# Revit family: PRD_AR_HndSntzrDspnsrs_MEDCAREDispenser_MEDC10S_MEDC10L 2
name_source: partatom
category: Specialty Equipment
units: mm (PartAtom-declared; Revit-internal decimal feet)

## family parameters
Cut with Voids When Loaded = No
Enable Cutting in Views = No
Host = Face
Maintain Annotation Orientation = No
OmniClass Number = 23.40.20.21.34
OmniClass Title = Soap Holders, Dispensers
Part Type = Normal
Room Calculation Point = No
Round Connector Dimension = Use Diameter
Shared = No

## types (2) — shared parameters
AccentColour = grey
AssetType = Fixed
BasicColour = stainless steel-look
BodyMaterial = PRD_AR_Plastic_Grey
Category = Pr_40_70_22_35, Hand sanitizer dispensers
Color = grey
Colour = grey
ContainerMaterial = PRD_AR_Plastic_White
Default Elevation = 1050 mm
Export Type to IFC As = IfcSanitaryTerminalType
FillingQuantity = 1000
FillingQuantityUOM = ml
Finish = satin finished
HousingMaterial = PRD_AR_StainlessSteel_SatinFinished
IfcExportAs = IfcSanitaryTerminalType
IfcExportType = USERDEFINED
LeverMaterial = PRD_AR_StainlessSteel_HighPolished
Manufacturer = KWC Group Management AG
ManufacturerName = KWC Group Management AG
ManufacturerURL = www.kwc-professional.com
Material = stainless steel
MaterialCode = 1.4301 Chrome Nickel steel V2A
MaterialThickness = 1.25 mm
NBSDescription = Hand sanitizer dispensers
NBSReference = 45-35-72/333
NominalWidth = 94 mm  [stored 0.308399 ft]
OverallWidth = 94 mm
ProductInformation = http://pim.kwc.com
Status = New
SurfaceFinish = satin finished
Type IFC Predefined Type = USERDEFINED
TypeOfConsumable = disinfectant and liquid soap
TypeOfFixing = screw
TypeOfMounting = wall mounting
TypeOfOperation = manual operation
URL = www.kwc-professional.com
Uniclass2015Code = Pr_40_70_22_35
Uniclass2015Title = Hand sanitizer dispensers
Uniclass2015Version = Products v1.38
Version = 1

## per-type parameters (varying)
| type | BIMObjectName | Description | Features | MEDC10L | MEDC10S | ModelNumber | Name | NominalDepth | NominalHeight | NominalLength | OverallDepth | OverallHeight | Size |
| MEDC10L | PRD_AR_HandSanitizerDispensers_MEDCAREDispenser_MEDC10L | MEDCARE dispenser for liquid soaps and disinfectants, for wall mounting, stainless steel housing (dishwasher safe up to 60 °C), satin finished surface, material thickness 1.25 mm, grey plastic outlet cover, for 1000 ml standard Euro-bottles to be provided by the client, with stainless steel operating lever 230 mm, including wall bracket and mounting material. | For liquid soaps and disinfectants for wall mounting, stainless steel housing. With stainless steel operating lever 230 mm. Disposable pump must be ordered separately. | Yes | No | 3600003341 | MEDCARE Dispenser for liquid soaps and disinfectants MEDC10L | 230 mm  [stored 0.754593 ft] | 321 mm  [stored 1.05315 ft] | 321 mm  [stored 1.05315 ft] | 230 mm | 321 mm | 94 x 321 x 230 mm (W x H x D) |
| MEDC10S | PRD_AR_HandSanitizerDispensers_MEDCAREDispenser_MEDC10S | MEDCARE dispenser for liquid soaps and disinfectants, for wall mounting, stainless steel housing (dishwasher safe up to 60 °C), satin finished surface, material thickness 1.25 mm, grey plastic outlet cover, for 1000 ml standard Euro-bottles to be provided by the client, with stainless steel operating lever 170 mm, including wall bracket and mounting material. | For liquid soaps and disinfectants for wall mounting, stainless steel housing. With stainless steel operating lever 170 mm. Disposable pump must be ordered separately. | No | Yes | 3600003343 | MEDCARE Dispenser for liquid soaps and disinfectants MEDC10S | 170 mm  [stored 0.557743 ft] | 341 mm | 341 mm | 170 mm | 341 mm | 94 x 341 x 170 mm (W x H x D) |

note: column(s) folded — value = type name in every type: Model, ModelReference

note: [stored X ft] marks values corroborated as IEEE doubles in the binary element streams (Revit-internal decimal feet)

## geometry (parser evidence)
native form markers: Sweep x6
no freeform markers — native parametric forms only
